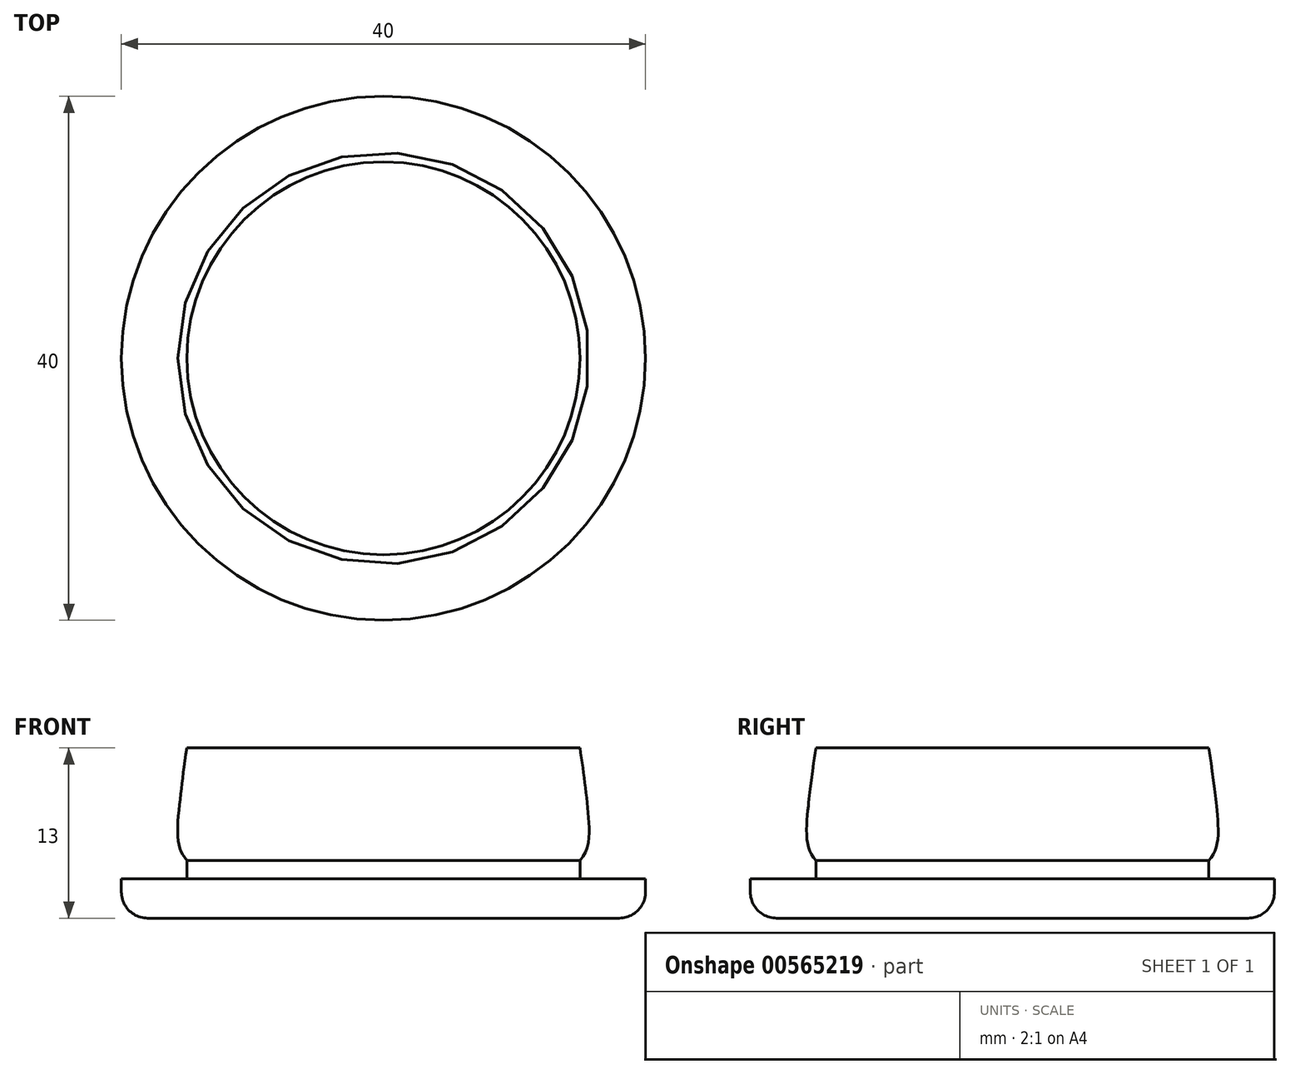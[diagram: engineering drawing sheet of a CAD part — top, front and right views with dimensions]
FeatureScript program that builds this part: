
annotation { "Feature Type Name" : "Feature", "Feature Type Description" : "" }
export const myFeature = defineFeature(function(context is Context, id is Id, definition is map)
    precondition{}
    {
        {
            var Q0;
            Q0=qCreatedBy(makeId("Front.planeOp"),FACE);
            var sketch = newSketch(context, id + "F0", { "sketchPlane" : qUnion([Q0])});
            skLineSegment(sketch, "E0", {"start": v(0, 19.7) * mm, "end": v(0, -26.7) * mm, "construction": true});
            skLineSegment(sketch, "E1", {"start": v(0, 13) * mm, "end": v(-15, 13) * mm});
            skLineSegment(sketch, "E2", {"start": v(-15, 4.4) * mm, "end": v(-15, 3) * mm});
            skLineSegment(sketch, "E3", {"start": v(-15, 3) * mm, "end": v(-20, 3) * mm});
            skLineSegment(sketch, "E4", {"start": v(-20, 3) * mm, "end": v(-20, 0) * mm});
            skLineSegment(sketch, "E5", {"start": v(-20, 0) * mm, "end": v(0, 0) * mm});
            skLineSegment(sketch, "E6", {"start": v(0, 0) * mm, "end": v(0, 13) * mm});
            skFitSpline(sketch, "E7", {"points": [v(-15, 4.4) * mm, v(-15.64, 5.8) * mm, v(-15.52, 9) * mm, v(-15, 13) * mm], "startDerivative": vector(-3.91, 5.05) * mm, "endDerivative": vector(1.79, 12.1) * mm});
            skSolve(sketch);
        }
        {
            var Q0;
            Q0=makeQuery(id+"F0.imprint","IMPRINT",FACE,{"disambiguationData":[TD([[makeQuery(id+"F0.imprint","IMPRINT",EDGE,{"derivedFrom":sQuery(id+"F0.wireOp",EDGE,"E1")}),1.0]])]});
            var Q1;
            Q1=sQuery(id+"F0.wireOp",EDGE,"E6");
            revolve(context, id + "F1", {"entities" : qUnion([Q0]), "axis" : qUnion([Q1]), "revolveType" : RevolveType.FULL});
        }
        {
            var Q0;
            Q0=makeQuery(id+"F1.opRevolve","SWEPT_EDGE",EDGE,{"disambiguationData":[OSD([sQuery(id+"F0.wireOp",EDGE,"E4"),sQuery(id+"F0.wireOp",EDGE,"E5")])]});
            fillet(context, id + "F2", {"entities" : qUnion([Q0]), "radius" : 2 * mm, "tangentPropagation" : true, "allowEdgeOverflow" : false});
        }
    });
